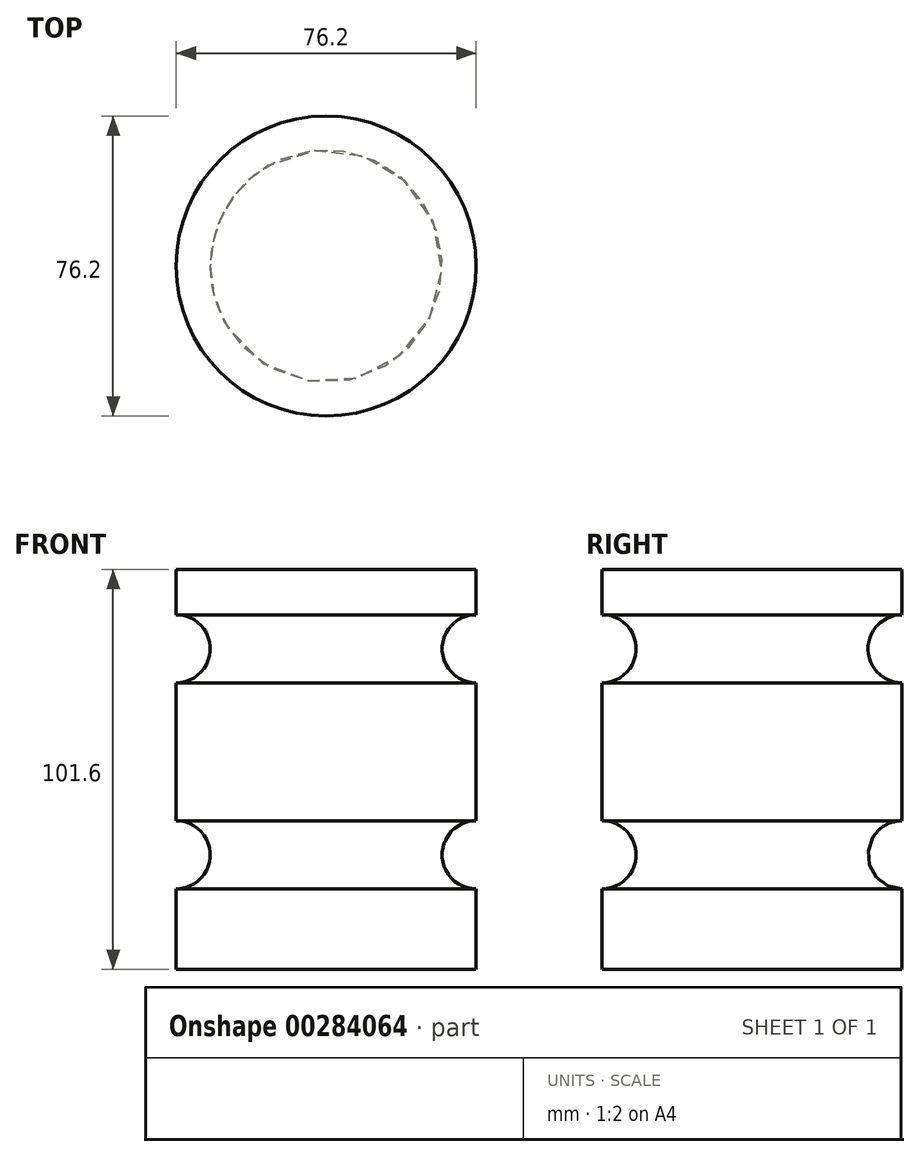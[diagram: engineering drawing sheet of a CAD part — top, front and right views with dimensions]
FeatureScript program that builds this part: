
annotation { "Feature Type Name" : "Feature", "Feature Type Description" : "" }
export const myFeature = defineFeature(function(context is Context, id is Id, definition is map)
    precondition{}
    {
        {
            var Q0;
            Q0=qCreatedBy(makeId("Front.planeOp"),FACE);
            var sketch = newSketch(context, id + "F0", { "sketchPlane" : qUnion([Q0])});
            skLineSegment(sketch, "E0.bottom", {"start": v(0, 0) * mm, "end": v(-38.1, 0) * mm});
            skLineSegment(sketch, "E0.top", {"start": v(0, 101.6) * mm, "end": v(-38.1, 101.6) * mm});
            skLineSegment(sketch, "E0.left", {"start": v(0, 0) * mm, "end": v(0, 20.46) * mm});
            skLineSegment(sketch, "E0.right", {"start": v(-38.1, 0) * mm, "end": v(-38.1, 101.6) * mm});
            skArc(sketch, "E1", {"start": v(0, 90.1) * mm, "mid": v(-8.64, 81.46) * mm, "end": v(0, 72.82) * mm});
            skArc(sketch, "E2", {"start": v(0, 37.75) * mm, "mid": v(-8.65, 29.1) * mm, "end": v(0, 20.46) * mm});
            skLineSegment(sketch, "E3.trimOffspring", {"start": v(0, 90.1) * mm, "end": v(0, 101.6) * mm});
            skLineSegment(sketch, "E4.trimOffspring", {"start": v(0, 37.75) * mm, "end": v(0, 72.82) * mm});
            skSolve(sketch);
        }
        {
            var Q0;
            Q0=makeQuery(id+"F0.imprint","IMPRINT",FACE,{"disambiguationData":[TD([[makeQuery(id+"F0.imprint","IMPRINT",EDGE,{"derivedFrom":sQuery(id+"F0.wireOp",EDGE,"E0.bottom")}),-1.0]])]});
            var Q1;
            Q1=sQuery(id+"F0.wireOp",EDGE,"E0.right");
            revolve(context, id + "F1", {"entities" : qUnion([Q0]), "axis" : qUnion([Q1]), "revolveType" : RevolveType.FULL});
        }
    });
